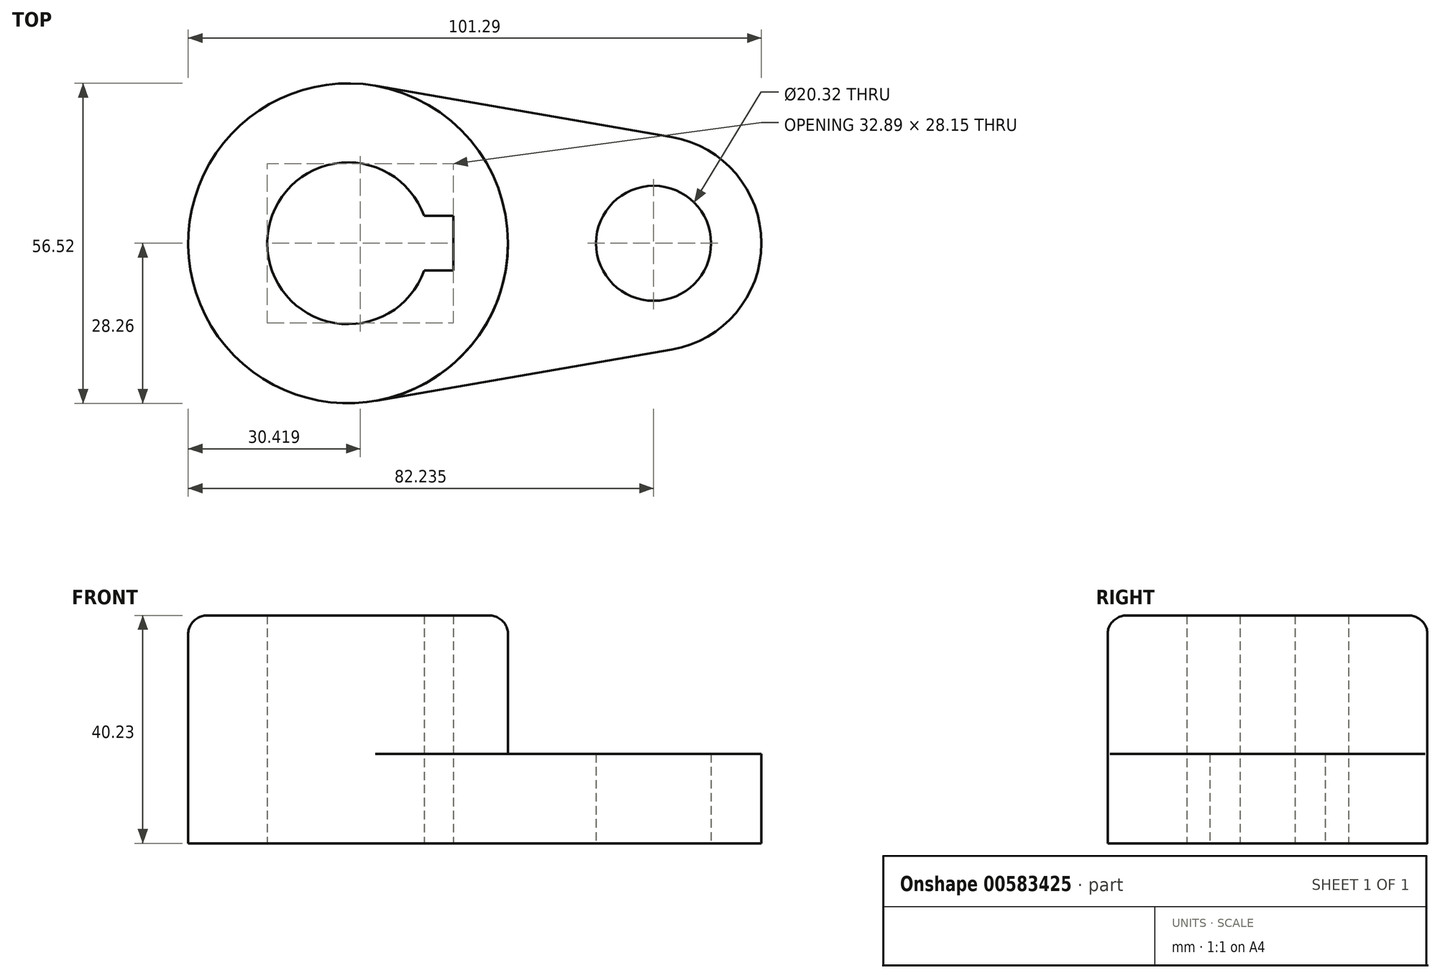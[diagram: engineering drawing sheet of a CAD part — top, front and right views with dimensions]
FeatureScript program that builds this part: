
annotation { "Feature Type Name" : "Feature", "Feature Type Description" : "" }
export const myFeature = defineFeature(function(context is Context, id is Id, definition is map)
    precondition{}
    {
        {
            var Q0;
            Q0=qCreatedBy(makeId("Top.planeOp"),FACE);
            var sketch = newSketch(context, id + "F0", { "sketchPlane" : qUnion([Q0])});
            skArc(sketch, "E0", {"start": v(13.45, 4.83) * mm, "mid": v(-14.29, 0) * mm, "end": v(13.45, -4.83) * mm});
            skCircle(sketch, "E1", {"center": v(0, 0) * mm, "radius": 28.26 * mm});
            skLineSegment(sketch, "E2", {"start": v(13.45, 4.83) * mm, "end": v(18.6, 4.83) * mm});
            skLineSegment(sketch, "E3.MirrorCS", {"start": v(13.45, -4.83) * mm, "end": v(18.6, -4.83) * mm});
            skLineSegment(sketch, "E4", {"start": v(18.6, -4.83) * mm, "end": v(18.6, 4.83) * mm});
            skCircle(sketch, "E5", {"center": v(53.98, 0) * mm, "radius": 10.16 * mm});
            skArc(sketch, "E6", {"start": v(57.22, -18.77) * mm, "mid": v(73.03, 0) * mm, "end": v(57.22, 18.77) * mm});
            skLineSegment(sketch, "E7", {"start": v(4.82, 27.84) * mm, "end": v(57.22, 18.77) * mm});
            skLineSegment(sketch, "E8", {"start": v(4.82, -27.84) * mm, "end": v(57.22, -18.77) * mm});
            skSolve(sketch);
        }
        {
            var Q0;
            Q0=makeQuery(id+"F0.imprint","IMPRINT",FACE,{"disambiguationData":[TD([[makeQuery(id+"F0.imprint","IMPRINT",EDGE,{"derivedFrom":sQuery(id+"F0.wireOp",EDGE,"E0")}),-1.0]])]});
            extrude(context, id + "F1", {"entities" : qUnion([Q0]), "depth" : 40.23 * mm, "offsetDistance" : 25.4 * mm});
        }
        {
            var Q0;
            Q0=makeQuery(id+"F0.imprint","IMPRINT",FACE,{"disambiguationData":[TD([[makeQuery(id+"F0.imprint","IMPRINT",EDGE,{"derivedFrom":sQuery(id+"F0.wireOp",EDGE,"E5")}),-1.0]])]});
            extrude(context, id + "F2", {"entities" : qUnion([Q0]), "operationType" : NewBodyOperationType.ADD, "depth" : 15.77 * mm, "offsetDistance" : 25.4 * mm});
        }
        {
            var Q0;
            Q0=makeQuery(id+"F1.opExtrude","CAP_EDGE",EDGE,{"disambiguationData":[OSD([sQuery(id+"F0.wireOp",EDGE,"E1")])],"isStart":false});
            fillet(context, id + "F3", {"entities" : qUnion([Q0]), "radius" : 3.3 * mm, "tangentPropagation" : true, "allowEdgeOverflow" : false});
        }
    });
